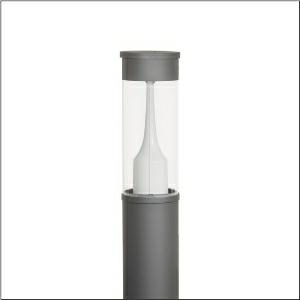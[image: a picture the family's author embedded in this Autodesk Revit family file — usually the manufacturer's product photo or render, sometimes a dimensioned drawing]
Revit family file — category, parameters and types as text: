
# Revit family: city-light_260_iq___p1_0a_5xa5295ff14h_c360
name_source: partatom
category: Lighting Fixtures
units: mm (PartAtom-declared; Revit-internal decimal feet)

## family parameters
Cut with Voids When Loaded = No
Host = Face
Light Source = No
Part Type = Normal
Room Calculation Point = No
Round Connector Dimension = Use Diameter
Shared = No

## types (1)
- --- (1 x LED, 1510 lm, 10.5 W, 3000K)
    Apparent Load = 11 VA
    CIE Flux Codes = 32 61 90 93 100
    Color Rendering = 70
    Color Temperature = 3000K
    Default Elevation = 1800 mm
    Description = City-Light 260 iQ, light pillar, Module 540 iQ-SR, primary light control with 3 zone facetted reflector, of plastic, silver coated, highly specular, structured, primary optical cover: cover, of PMMA, transparent, light distribution: P1.0a, primary light characteristic: strongly asymmetric, LED, High Power LED, rated luminous flux: 1.510lm, luminous efficacy: 144lm/W, light colour: 730, colour temperature: 3000K, control gear: ECG iQ, control: Auto-Match, Temp-Guard, Lumen-Switch, Night-Set, Smart-Wire, Light-Fading, Desk-Remote (wireless, voltage-free reading and setting of iQ features in the workshop via application-optimized NFC function/RFID function), optimised constant luminous flux control (CLO 2.0), Street-Remote, presetting dimming logarithmic, with terminal, 6-pole, max. 2.5mm², mains connection: 220..240V, AC, 50/60Hz, start of lifetime: 11W, end of lifetime: 11W, reduction: 5W, luminaire housing, cylindrical, of extruded aluminium section, coated, Siteco® metallic grey (DB 702S), length: 2.600mm, diameter: 200mm, Module 540 iQ-SR, traffic white (RAL 9016), equipment: standard, protection rating (complete): IP65, insulation class (complete): insulation class II (safety insulation), certification: CE, ENEC, VDE, packaging unit: 1 piece

Light Distribution: P1.0a
    Height = 500 mm
    Lamp = 1 x LED
    Lamp Light Flux = 1510 lm
    Lamp Power = 10.5 W
    Lamp count = 1
    Length = 200 mm  [stored 0.656168 ft]
    Luminous efficacy = 144 lm/W
    Manufacturer = Siteco
    ModVariant = No
    Model = 5XA5295FF14H
    Number of Poles = 1
    OnlyDefault = Yes
    Power Factor = 1
    Product Name = City-Light 260 iQ | P1.0a
    Product group = light pillar | pylon top
    ProductGroupID = 6103
    Protection Class = Protection class II
    Protection Degree = IP 65
    RLX_Detail_Level = 1
    RlxData = <blob elided: 52501 chars, md5=09401595>
    Socket = socket
    Standby Power = 0 W
    System Light Flux = 1510 lm
    System Power = 11 W
    Type Comments = factory setting: luminous flux: 100 % | dim-lin: 254 | 419 mA
    Type Image = l_1006918.jpg
    URL = http://relux.com
    VarID = @adj_070743
    Voltage = 0 V
    Weight = 0.00 kg
    Width = 0 mm  [stored 0 ft]

note: [stored X ft] marks values corroborated as IEEE doubles in the binary element streams (Revit-internal decimal feet)

## geometry (parser evidence)
native form markers: Blend x4, Sweep x10
no freeform markers — native parametric forms only
